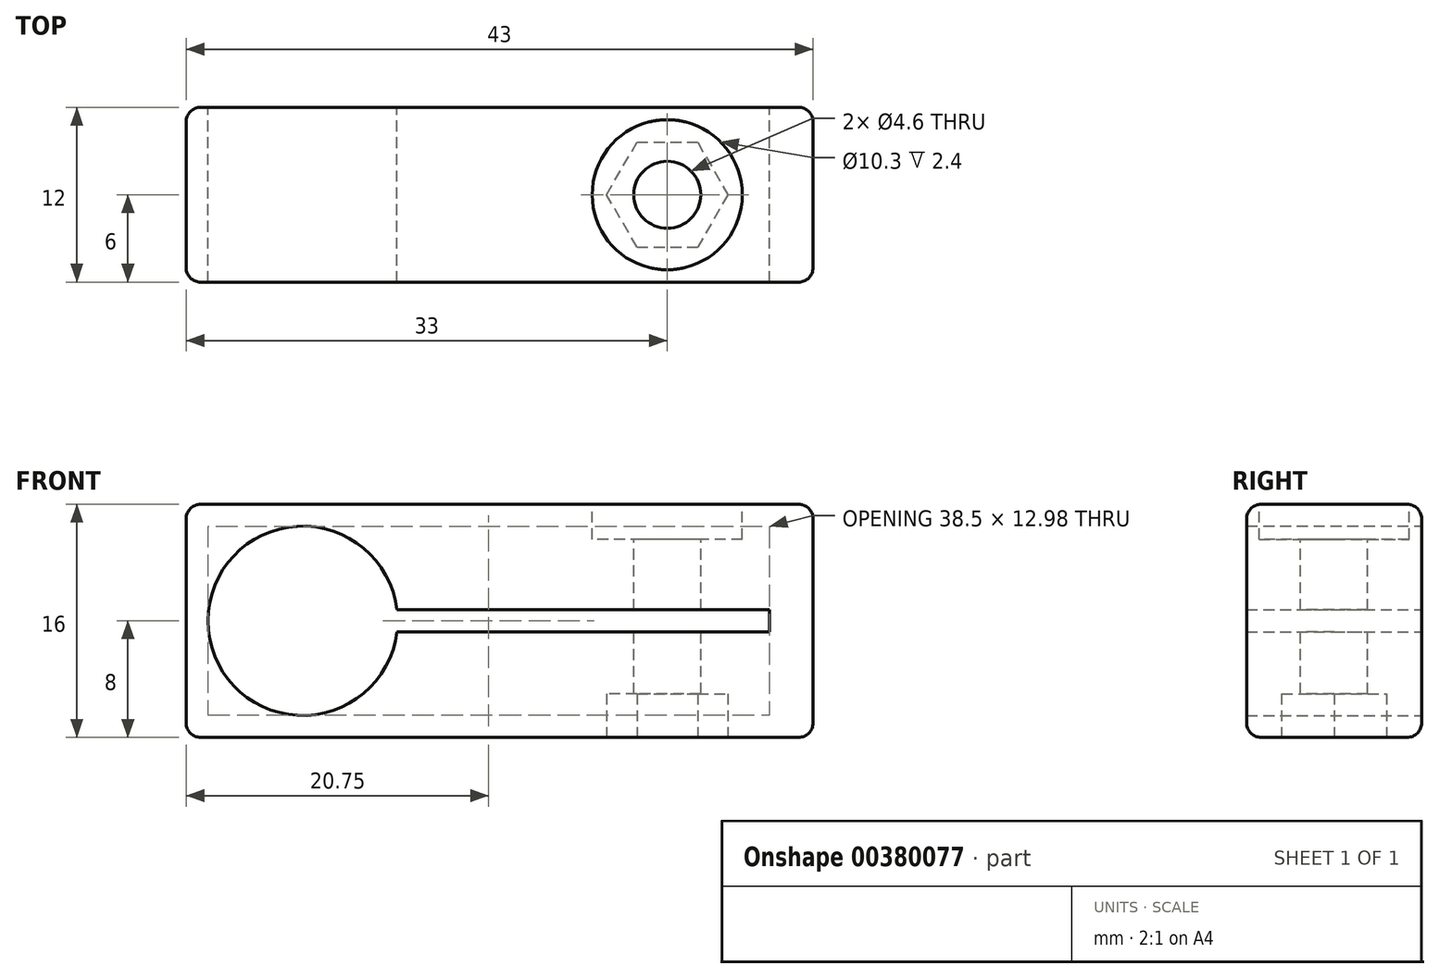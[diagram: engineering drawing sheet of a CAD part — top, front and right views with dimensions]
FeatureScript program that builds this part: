
annotation { "Feature Type Name" : "Feature", "Feature Type Description" : "" }
export const myFeature = defineFeature(function(context is Context, id is Id, definition is map)
    precondition{}
    {
        {
            var Q0;
            Q0=qCreatedBy(makeId("Front.planeOp"),FACE);
            var sketch = newSketch(context, id + "F0", { "sketchPlane" : qUnion([Q0])});
            skLineSegment(sketch, "E0.bottom", {"start": v(-21.5, 8) * mm, "end": v(21.5, 8) * mm});
            skLineSegment(sketch, "E0.top", {"start": v(-21.5, -8) * mm, "end": v(21.5, -8) * mm});
            skLineSegment(sketch, "E0.left", {"start": v(-21.5, 8) * mm, "end": v(-21.5, -8) * mm});
            skLineSegment(sketch, "E0.right", {"start": v(21.5, 8) * mm, "end": v(21.5, -8) * mm});
            skPoint(sketch, "E0.middle", {"position": v(0, 0) * mm});
            skArc(sketch, "E1", {"start": v(-7.04, 0.75) * mm, "mid": v(-20, 0) * mm, "end": v(-7.04, -0.75) * mm});
            skPoint(sketch, "E1.centerSnap0", {"position": v(-21.5, 0) * mm});
            skLineSegment(sketch, "E2", {"start": v(-7.04, 0.75) * mm, "end": v(18.5, 0.75) * mm});
            skLineSegment(sketch, "E3", {"start": v(18.5, 0.75) * mm, "end": v(18.5, -0.75) * mm});
            skLineSegment(sketch, "E4", {"start": v(18.5, -0.75) * mm, "end": v(-7.04, -0.75) * mm});
            skPoint(sketch, "E5", {"position": v(18.5, 0) * mm});
            skSolve(sketch);
        }
        {
            var Q0;
            Q0=makeQuery(id+"F0.imprint","IMPRINT",FACE,{"disambiguationData":[TD([[makeQuery(id+"F0.imprint","IMPRINT",EDGE,{"derivedFrom":sQuery(id+"F0.wireOp",EDGE,"E0.bottom")}),-1.0]])]});
            extrude(context, id + "F1", {"entities" : qUnion([Q0]), "endBound" : BoundingType.SYMMETRIC, "depth" : 12 * mm});
        }
        {
            var Q0;
            Q0=makeQuery(id+"F1.opExtrude","SWEPT_FACE",FACE,{"disambiguationData":[OSD([sQuery(id+"F0.wireOp",EDGE,"E0.bottom")])]});
            var sketch = newSketch(context, id + "F2", { "sketchPlane" : qUnion([Q0])});
            skCircle(sketch, "E6", {"center": v(11.5, 0) * mm, "radius": 2.3 * mm});
            skCircle(sketch, "E7", {"center": v(11.5, 0) * mm, "radius": 5.15 * mm});
            skSolve(sketch);
        }
        {
            var Q0;
            Q0=makeQuery(id+"F2.imprint","IMPRINT",FACE,{"disambiguationData":[TD([[makeQuery(id+"F2.imprint","IMPRINT",EDGE,{"derivedFrom":sQuery(id+"F2.wireOp",EDGE,"E6")}),1.0]])]});
            var Q1;
            Q1=makeQuery(id+"F1.opExtrude","SWEPT_FACE",FACE,{"disambiguationData":[OSD([sQuery(id+"F0.wireOp",EDGE,"E0.top")])]});
            extrude(context, id + "F3", {"entities" : qUnion([Q0]), "operationType" : NewBodyOperationType.REMOVE, "endBound" : BoundingType.UP_TO_SURFACE, "oppositeDirection" : true, "endBoundEntityFace" : qUnion([Q1]), "depth" : 25 * mm});
        }
        {
            var Q0;
            Q0=makeQuery(id+"F2.imprint","IMPRINT",FACE,{"disambiguationData":[TD([[makeQuery(id+"F2.imprint","IMPRINT",EDGE,{"derivedFrom":sQuery(id+"F2.wireOp",EDGE,"E6")}),-1.0]])]});
            extrude(context, id + "F4", {"entities" : qUnion([Q0]), "operationType" : NewBodyOperationType.REMOVE, "oppositeDirection" : true, "depth" : 2.4 * mm});
        }
        {
            var Q0;
            Q0=makeQuery(id+"F1.opExtrude","SWEPT_FACE",FACE,{"disambiguationData":[OSD([sQuery(id+"F0.wireOp",EDGE,"E0.top")])]});
            var sketch = newSketch(context, id + "F5", { "sketchPlane" : qUnion([Q0])});
            skPoint(sketch, "E8", {"position": v(11.5, 0) * mm});
            skCircle(sketch, "E9", {"center": v(11.5, 0) * mm, "radius": 3.6 * mm, "construction": true});
            skLineSegment(sketch, "E10", {"start": v(9.42, 3.6) * mm, "end": v(13.58, 3.6) * mm});
            skLineSegment(sketch, "E11", {"start": v(9.42, 3.6) * mm, "end": v(7.34, 0) * mm});
            skLineSegment(sketch, "E12", {"start": v(7.34, 0) * mm, "end": v(9.42, -3.6) * mm});
            skLineSegment(sketch, "E13", {"start": v(9.42, -3.6) * mm, "end": v(13.58, -3.6) * mm});
            skLineSegment(sketch, "E14", {"start": v(13.58, -3.6) * mm, "end": v(15.66, 0) * mm});
            skLineSegment(sketch, "E15", {"start": v(15.66, 0) * mm, "end": v(13.58, 3.6) * mm});
            skSolve(sketch);
        }
        {
            var Q0;
            Q0=makeQuery(id+"F5.imprint","IMPRINT",FACE,{"disambiguationData":[TD([[makeQuery(id+"F5.imprint","IMPRINT",EDGE,{"derivedFrom":sQuery(id+"F5.wireOp",EDGE,"E10")}),-1.0]])]});
            extrude(context, id + "F6", {"entities" : qUnion([Q0]), "operationType" : NewBodyOperationType.REMOVE, "oppositeDirection" : true, "depth" : 3 * mm});
        }
        {
            var Q0;
            Q0=makeQuery(id+"F1.opExtrude","SWEPT_EDGE",EDGE,{"disambiguationData":[OSD([sQuery(id+"F0.wireOp",EDGE,"E0.top"),sQuery(id+"F0.wireOp",EDGE,"E0.left")])]});
            var Q1;
            Q1=makeQuery(id+"F1.opExtrude","CAP_EDGE",EDGE,{"disambiguationData":[OSD([sQuery(id+"F0.wireOp",EDGE,"E0.top")])],"isStart":false});
            var Q2;
            Q2=makeQuery(id+"F1.opExtrude","CAP_EDGE",EDGE,{"disambiguationData":[OSD([sQuery(id+"F0.wireOp",EDGE,"E0.top")])],"isStart":true});
            var Q3;
            Q3=makeQuery(id+"F1.opExtrude","SWEPT_EDGE",EDGE,{"disambiguationData":[OSD([sQuery(id+"F0.wireOp",EDGE,"E0.top"),sQuery(id+"F0.wireOp",EDGE,"E0.right")])]});
            var Q4;
            Q4=makeQuery(id+"F1.opExtrude","CAP_EDGE",EDGE,{"disambiguationData":[OSD([sQuery(id+"F0.wireOp",EDGE,"E0.right")])],"isStart":true});
            var Q5;
            Q5=makeQuery(id+"F1.opExtrude","CAP_EDGE",EDGE,{"disambiguationData":[OSD([sQuery(id+"F0.wireOp",EDGE,"E0.right")])],"isStart":false});
            var Q6;
            Q6=makeQuery(id+"F1.opExtrude","CAP_EDGE",EDGE,{"disambiguationData":[OSD([sQuery(id+"F0.wireOp",EDGE,"E0.left")])],"isStart":true});
            var Q7;
            Q7=makeQuery(id+"F1.opExtrude","CAP_EDGE",EDGE,{"disambiguationData":[OSD([sQuery(id+"F0.wireOp",EDGE,"E0.left")])],"isStart":false});
            var Q8;
            Q8=makeQuery(id+"F1.opExtrude","SWEPT_EDGE",EDGE,{"disambiguationData":[OSD([sQuery(id+"F0.wireOp",EDGE,"E0.bottom"),sQuery(id+"F0.wireOp",EDGE,"E0.left")])]});
            var Q9;
            Q9=makeQuery(id+"F1.opExtrude","CAP_EDGE",EDGE,{"disambiguationData":[OSD([sQuery(id+"F0.wireOp",EDGE,"E0.bottom")])],"isStart":false});
            var Q10;
            Q10=makeQuery(id+"F1.opExtrude","CAP_EDGE",EDGE,{"disambiguationData":[OSD([sQuery(id+"F0.wireOp",EDGE,"E0.bottom")])],"isStart":true});
            var Q11;
            Q11=makeQuery(id+"F1.opExtrude","SWEPT_EDGE",EDGE,{"disambiguationData":[OSD([sQuery(id+"F0.wireOp",EDGE,"E0.bottom"),sQuery(id+"F0.wireOp",EDGE,"E0.right")])]});
            fillet(context, id + "F7", {"entities" : qUnion([Q0, Q1, Q2, Q3, Q4, Q5, Q6, Q7, Q8, Q9, Q10, Q11]), "radius" : 1 * mm, "tangentPropagation" : true, "allowEdgeOverflow" : false});
        }
    });
